# Revit family: TY5151
name_source: partatom
category: Sprinklers
revit_build: Autodesk Revit 2016 (Build: 20150220_1215(x64)
units: mm (PartAtom-declared; Revit-internal decimal feet)

## family parameters
Always vertical = Yes
Cut with Voids When Loaded = No
Maintain Annotation Orientation = No
OmniClass Number = 23.65.70.17.11.24
OmniClass Title = Fire Fighting Sprinkler Heads
Part Type = Normal
Room Calculation Point = No
Round Connector Dimension = Use Diameter
Shared = No
Work Plane-Based = No

## types (15) — shared parameters
COBie = Yes
COBie.Component.Name = Sprinklers:Upright_SIN
COBie.Type = Yes
COBie.Type.AssetType = Fixed
COBie.Type.Category = Pr_70_55_97_84:Sprinklers
COBie.Type.DurationUnit = year
COBie.Type.Manufacturer = Tyco Fire Protection Products
COBie.Type.Material = Bronze
COBie.Type.Shape = Cylinder
COBie.Type.Size = 3/4"(DN20)
COBie.Type.WarrantyGuarantorParts = http://tycofsbp.com
Coverage = Standard
K-Factor = 159.8191
Manufacturer = Tyco Fire Protection Products
Manufacturer URL = www.tyco-fire.com
Model = ELO-231B
Nominal Diameter 1 = 20 mm
Orifice = Extra Large
Orifice Size = 16 mm
Outside Diameter 1 = 27 mm
Response = Standard
SIN No = TY5151
Takeout 1 = 71 mm
Technical Data Sheet No = TFP342
zero-valued in all types: COBie.Type.NominalHeight, COBie.Type.NominalLength, COBie.Type.NominalWidth, COBie.Type.ReplacementCost, Style Id

## per-type parameters (varying)
| type | COBie.Component.Description | COBie.Type.Colour | COBie.Type.Finish | COBie.Type.ModelNumber | COBie.Type.ModelReference | COBie.Type.WarrantyDescription | Part No | Temperature Rating |
| ELO-231B Wet Upright_Yellow_155  68.3°C K160 DN20 NPT Br_50-510-1-155 | ELO-231B Wet Upright  68.3°C K160 DN20 NPT Br | Yellow | Natural Brass | 50-510-1-155 | ELO-231B Wet Upright  68.3°C K160 DN20 NPT Br |  | 50-510-1-155 | 68 °C |
| ELO-231B Wet Upright_Yellow_200  93.3°C K160 DN20 NPT Br_50-510-1-200 | ELO-231B Wet Upright  93.3°C K160 DN20 NPT Br | Yellow | Natural Brass | 50-510-1-200 | ELO-231B Wet Upright  93.3°C K160 DN20 NPT Br | na/ | 50-510-1-200 | 93 °C |
| ELO-231B Wet Upright_Yellow_286  141.1°C K160 DN20 NPT Br_50-510-1-286 | ELO-231B Wet Upright  141.1°C K160 DN20 NPT Br | Yellow | Natural Brass | 50-510-1-286 | ELO-231B Wet Upright  141.1°C K160 DN20 NPT Br |  | 50-510-1-286 | 141 °C |
| ELO-231B Wet Upright_Gray_155  68.3°C K160 DN20 NPT Wx_50-510-6-155 | ELO-231B Wet Upright  68.3°C K160 DN20 NPT Wx | Gray | Wax Coated | 50-510-6-155 | ELO-231B Wet Upright  68.3°C K160 DN20 NPT Wx |  | 50-510-6-155 | 68 °C |
| ELO-231B Wet Upright_Gray_200  93.3°C K160 DN20 NPT Wx_50-510-6-200 | ELO-231B Wet Upright  93.3°C K160 DN20 NPT Wx | Gray | Wax Coated | 50-510-6-200 | ELO-231B Wet Upright  93.3°C K160 DN20 NPT Wx |  | 50-510-6-200 | 93 °C |
| ELO-231B Wet Upright_Gray_286  141.1°C K160 DN20 NPT Wx_50-510-6-286 | ELO-231B Wet Upright  141.1°C K160 DN20 NPT Wx | Gray | Wax Coated | 50-510-6-286 | ELO-231B Wet Upright  141.1°C K160 DN20 NPT Wx |  | 50-510-6-286 | 141 °C |
| ELO-231B Wet Upright_Gray_155  68.3°C K160 DN20 NPT Lead_50-510-7-155 | ELO-231B Wet Upright  68.3°C K160 DN20 NPT Lead | Gray | Lead Coated | 50-510-7-155 | ELO-231B Wet Upright  68.3°C K160 DN20 NPT Lead |  | 50-510-7-155 | 68 °C |
| ELO-231B Wet Upright_Gray_200  93.3°C K160 DN20 NPT Lead_50-510-7-200 | ELO-231B Wet Upright  93.3°C K160 DN20 NPT Lead | Gray | Lead Coated | 50-510-7-200 | ELO-231B Wet Upright  93.3°C K160 DN20 NPT Lead |  | 50-510-7-200 | 93 °C |
| ELO-231B Wet Upright_Gray_286  141.1°C K160 DN20 NPT Lead_50-510-7-286 | ELO-231B Wet Upright  141.1°C K160 DN20 NPT Lead | Gray | Lead Coated | 50-510-7-286 | ELO-231B Wet Upright  141.1°C K160 DN20 NPT Lead |  | 50-510-7-286 | 141 °C |
| ELO-231B Wet Upright_Gray_155  68.3°C K160 DN20 NPT WoL_50-510-8-155 | ELO-231B Wet Upright  68.3°C K160 DN20 NPT WoL | Gray | Wax Over Lead Coated | 50-510-8-155 | ELO-231B Wet Upright  68.3°C K160 DN20 NPT WoL |  | 50-510-8-155 | 68 °C |
| ELO-231B Wet Upright_Gray_200  93.3°C K160 DN20 NPT WoL_50-510-8-200 | ELO-231B Wet Upright  93.3°C K160 DN20 NPT WoL | Gray | Wax Over Lead Coated | 50-510-8-200 | ELO-231B Wet Upright  93.3°C K160 DN20 NPT WoL |  | 50-510-8-200 | 93 °C |
| ELO-231B Wet Upright_Gray_286  141.1°C K160 DN20 NPT WoL_50-510-8-286 | ELO-231B Wet Upright  141.1°C K160 DN20 NPT WoL | Gray | Wax Over Lead Coared | 50-510-8-286 | ELO-231B Wet Upright  141.1°C K160 DN20 NPT WoL |  | 50-510-8-286 | 141 °C |
| ELO-231B Wet Upright_Silver_155  68.3°C K160 DN20 NPT Chr_50-510-9-155 | ELO-231B Wet Upright  68.3°C K160 DN20 NPT Chr | Silver | Chrome Plated | 50-510-9-155 | ELO-231B Wet Upright  68.3°C K160 DN20 NPT Chr |  | 50-510-9-155 | 68 °C |
| ELO-231B Wet Upright_Silver_200  93.3°C K160 DN20 NPT Chr_50-510-9-200 | ELO-231B Wet Upright  93.3°C K160 DN20 NPT Chr | Silver | Chrome Plated | 50-510-9-200 | ELO-231B Wet Upright  93.3°C K160 DN20 NPT Chr |  | 50-510-9-200 | 93 °C |
| ELO-231B Wet Upright_Silver_286  141.1°C K160 DN20 NPT Chr_50-510-9-286 | ELO-231B Wet Upright  141.1°C K160 DN20 NPT Chr | Silver | Chrome PLated | 50-510-9-286 | ELO-231B Wet Upright  141.1°C K160 DN20 NPT Chr |  | 50-510-9-286 | 141 °C |

note: column(s) folded — value = type name in every type: Description

## geometry (parser evidence)
native form markers: Blend x2, Sweep x66
no freeform markers — native parametric forms only
